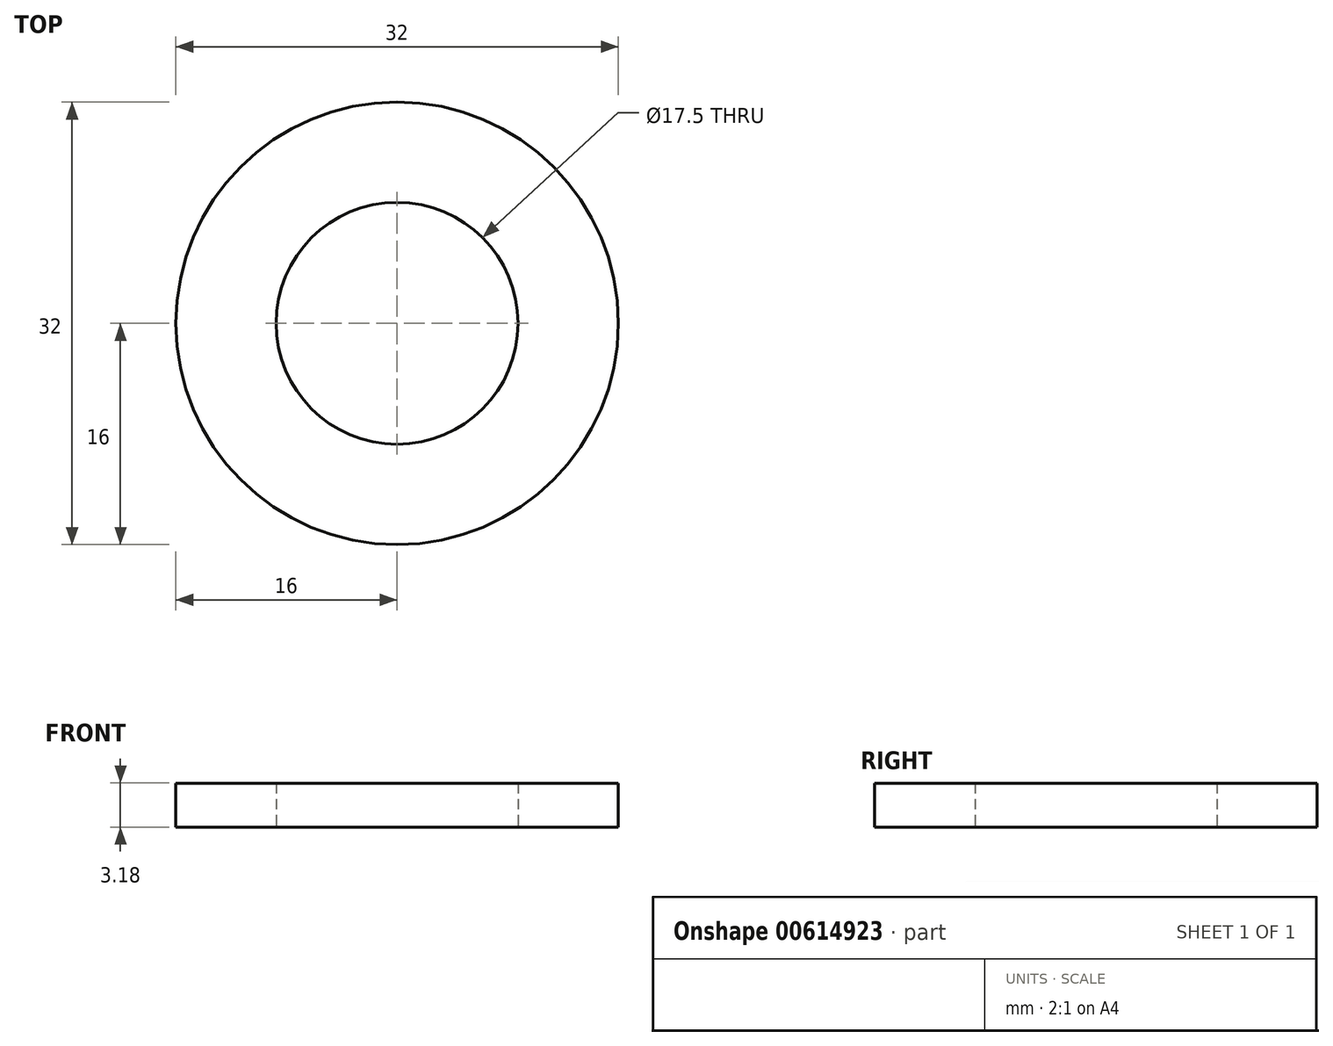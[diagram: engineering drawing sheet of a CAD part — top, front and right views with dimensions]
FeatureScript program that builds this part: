
annotation { "Feature Type Name" : "Feature", "Feature Type Description" : "" }
export const myFeature = defineFeature(function(context is Context, id is Id, definition is map)
    precondition{}
    {
        {
            var Q0;
            Q0=qCreatedBy(makeId("Top.planeOp"),FACE);
            var sketch = newSketch(context, id + "F0", { "sketchPlane" : qUnion([Q0])});
            skCircle(sketch, "E0", {"center": v(0, 0) * mm, "radius": 8.75 * mm});
            skCircle(sketch, "E1", {"center": v(0, 0) * mm, "radius": 16 * mm});
            skSolve(sketch);
        }
        {
            var Q0;
            Q0 = qSketchRegion(id + "F0", true);
            extrude(context, id + "F1", {"entities" : qUnion([Q0]), "depth" : 3.17 * mm, "offsetDistance" : 25 * mm});
        }
    });
